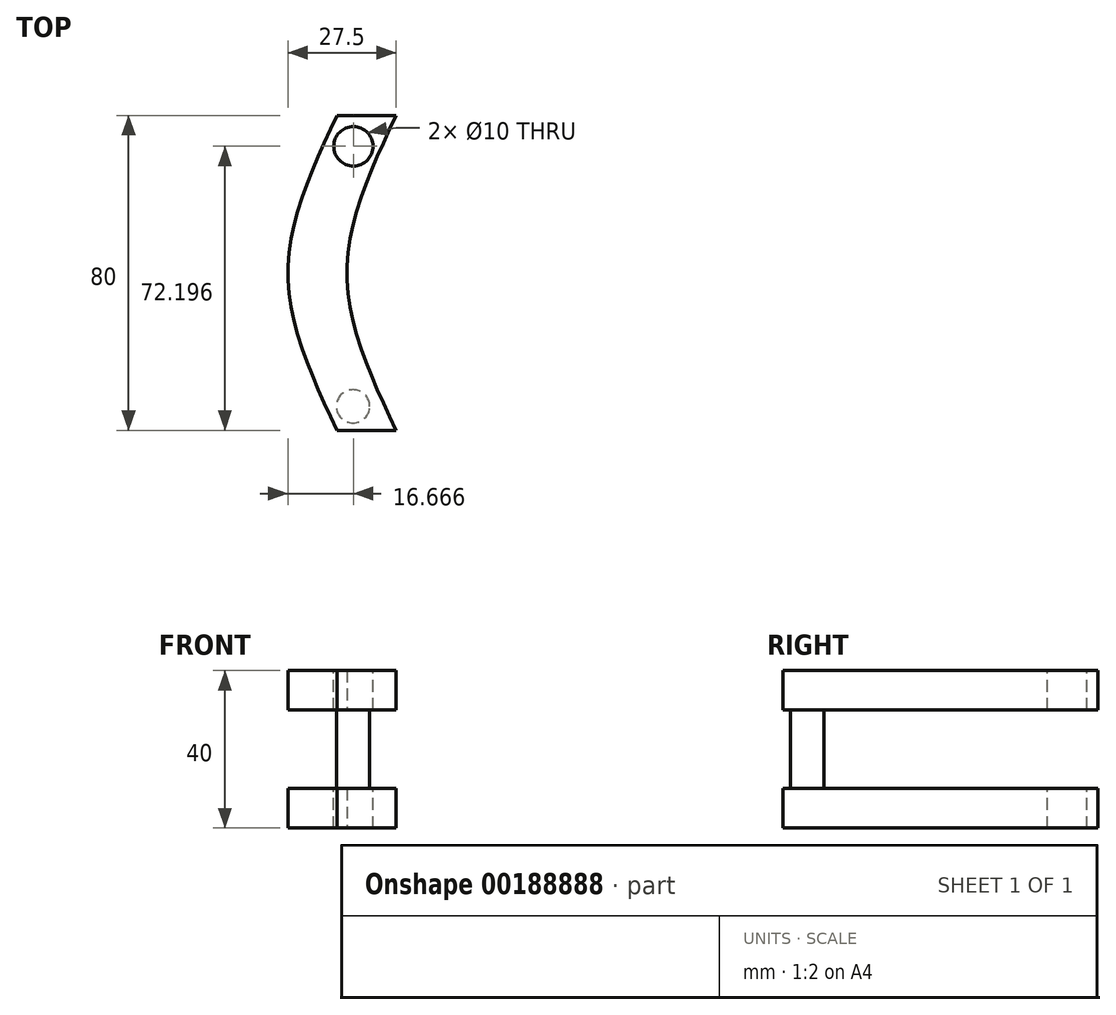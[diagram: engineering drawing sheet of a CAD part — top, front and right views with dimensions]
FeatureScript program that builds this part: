
annotation { "Feature Type Name" : "Feature", "Feature Type Description" : "" }
export const myFeature = defineFeature(function(context is Context, id is Id, definition is map)
    precondition{}
    {
        {
            var Q0;
            Q0=qCreatedBy(makeId("Front.planeOp"),FACE);
            var sketch = newSketch(context, id + "F0", { "sketchPlane" : qUnion([Q0])});
            skLineSegment(sketch, "E0.bottom", {"start": v(7.5, 10) * mm, "end": v(-7.5, 10) * mm});
            skLineSegment(sketch, "E0.top", {"start": v(7.5, 20) * mm, "end": v(-7.5, 20) * mm});
            skLineSegment(sketch, "E0.left", {"start": v(7.5, 10) * mm, "end": v(7.5, 20) * mm});
            skLineSegment(sketch, "E0.right", {"start": v(-7.5, 10) * mm, "end": v(-7.5, 20) * mm});
            skPoint(sketch, "E0.middle", {"position": v(0, 15) * mm});
            skLineSegment(sketch, "E1.bottom", {"start": v(7.5, -20) * mm, "end": v(-7.5, -20) * mm});
            skLineSegment(sketch, "E1.top", {"start": v(7.5, -10) * mm, "end": v(-7.5, -10) * mm});
            skLineSegment(sketch, "E1.left", {"start": v(7.5, -20) * mm, "end": v(7.5, -10) * mm});
            skLineSegment(sketch, "E1.right", {"start": v(-7.5, -20) * mm, "end": v(-7.5, -10) * mm});
            skPoint(sketch, "E1.middle", {"position": v(0, -15) * mm});
            skSolve(sketch);
        }
        {
            var Q0;
            Q0=qCreatedBy(makeId("Front.planeOp"),FACE);
            cPlane(context, id + "F1", {"entities" : qUnion([Q0]), "cplaneType" : CPlaneType.OFFSET, "offset" : 40 * mm, "width" : 150 * mm, "height" : 150 * mm});
        }
        {
            var Q0;
            Q0=qCreatedBy(id+"F1.planeOp",FACE);
            var sketch = newSketch(context, id + "F2", { "sketchPlane" : qUnion([Q0])});
            skLineSegment(sketch, "E2.bottom", {"start": v(-20, 10) * mm, "end": v(-5, 10) * mm});
            skLineSegment(sketch, "E2.top", {"start": v(-20, 20) * mm, "end": v(-5, 20) * mm});
            skLineSegment(sketch, "E2.left", {"start": v(-20, 10) * mm, "end": v(-20, 20) * mm});
            skLineSegment(sketch, "E2.right", {"start": v(-5, 10) * mm, "end": v(-5, 20) * mm});
            skPoint(sketch, "E2.middle", {"position": v(-12.5, 15) * mm});
            skLineSegment(sketch, "E3.bottom", {"start": v(-5, -20) * mm, "end": v(-20, -20) * mm});
            skLineSegment(sketch, "E3.top", {"start": v(-5, -10) * mm, "end": v(-20, -10) * mm});
            skLineSegment(sketch, "E3.left", {"start": v(-5, -20) * mm, "end": v(-5, -10) * mm});
            skLineSegment(sketch, "E3.right", {"start": v(-20, -20) * mm, "end": v(-20, -10) * mm});
            skPoint(sketch, "E3.middle", {"position": v(-12.5, -15) * mm});
            skSolve(sketch);
        }
        {
            var Q0;
            Q0=qCreatedBy(id+"F1.planeOp",FACE);
            cPlane(context, id + "F3", {"entities" : qUnion([Q0]), "cplaneType" : CPlaneType.OFFSET, "offset" : 40 * mm, "width" : 150 * mm, "height" : 150 * mm});
        }
        {
            var Q0;
            Q0=qCreatedBy(id+"F3.planeOp",FACE);
            var sketch = newSketch(context, id + "F4", { "sketchPlane" : qUnion([Q0])});
            skLineSegment(sketch, "E4.bottom", {"start": v(7.5, 10) * mm, "end": v(-7.5, 10) * mm});
            skLineSegment(sketch, "E4.top", {"start": v(7.5, 20) * mm, "end": v(-7.5, 20) * mm});
            skLineSegment(sketch, "E4.left", {"start": v(7.5, 10) * mm, "end": v(7.5, 20) * mm});
            skLineSegment(sketch, "E4.right", {"start": v(-7.5, 10) * mm, "end": v(-7.5, 20) * mm});
            skPoint(sketch, "E4.middle", {"position": v(0, 15) * mm});
            skLineSegment(sketch, "E5.bottom", {"start": v(7.5, -20) * mm, "end": v(-7.5, -20) * mm});
            skLineSegment(sketch, "E5.top", {"start": v(7.5, -10) * mm, "end": v(-7.5, -10) * mm});
            skLineSegment(sketch, "E5.left", {"start": v(7.5, -20) * mm, "end": v(7.5, -10) * mm});
            skLineSegment(sketch, "E5.right", {"start": v(-7.5, -20) * mm, "end": v(-7.5, -10) * mm});
            skPoint(sketch, "E5.middle", {"position": v(0, -15) * mm});
            skSolve(sketch);
        }
        {
            var Q0;
            Q0=makeQuery(id+"F4.imprint","IMPRINT",FACE,{"disambiguationData":[TD([[makeQuery(id+"F4.imprint","IMPRINT",EDGE,{"derivedFrom":sQuery(id+"F4.wireOp",EDGE,"E4.bottom")}),-1.0]])]});
            var Q1;
            Q1=makeQuery(id+"F2.imprint","IMPRINT",FACE,{"disambiguationData":[TD([[makeQuery(id+"F2.imprint","IMPRINT",EDGE,{"derivedFrom":sQuery(id+"F2.wireOp",EDGE,"E2.bottom")}),1.0]])]});
            var Q2;
            Q2=makeQuery(id+"F0.imprint","IMPRINT",FACE,{"disambiguationData":[TD([[makeQuery(id+"F0.imprint","IMPRINT",EDGE,{"derivedFrom":sQuery(id+"F0.wireOp",EDGE,"E0.bottom")}),-1.0]])]});
            loft(context, id + "F5", {"sheetProfilesArray" : [{ "sheetProfileEntities" : qUnion([Q0]) }, { "sheetProfileEntities" : qUnion([Q1]) }, { "sheetProfileEntities" : qUnion([Q2]) }]});
        }
        {
            var Q0;
            Q0=makeQuery(id+"F4.imprint","IMPRINT",FACE,{"disambiguationData":[TD([[makeQuery(id+"F4.imprint","IMPRINT",EDGE,{"derivedFrom":sQuery(id+"F4.wireOp",EDGE,"E5.bottom")}),-1.0]])]});
            var Q1;
            Q1=makeQuery(id+"F2.imprint","IMPRINT",FACE,{"disambiguationData":[TD([[makeQuery(id+"F2.imprint","IMPRINT",EDGE,{"derivedFrom":sQuery(id+"F2.wireOp",EDGE,"E3.bottom")}),-1.0]])]});
            var Q2;
            Q2=makeQuery(id+"F0.imprint","IMPRINT",FACE,{"disambiguationData":[TD([[makeQuery(id+"F0.imprint","IMPRINT",EDGE,{"derivedFrom":sQuery(id+"F0.wireOp",EDGE,"E1.bottom")}),-1.0]])]});
            loft(context, id + "F6", {"sheetProfilesArray" : [{ "sheetProfileEntities" : qUnion([Q0]) }, { "sheetProfileEntities" : qUnion([Q1]) }, { "sheetProfileEntities" : qUnion([Q2]) }]});
        }
        {
            var Q0;
            Q0=makeQuery(id+"F5.opLoft","SWEPT_FACE",FACE,{"disambiguationData":[OSD([sQuery(id+"F2.wireOp",EDGE,"E2.top"),sQuery(id+"F2.wireOp",EDGE,"E2.left"),sQuery(id+"F2.wireOp",EDGE,"E2.right"),sQuery(id+"F4.wireOp",EDGE,"E4.top"),sQuery(id+"F4.wireOp",EDGE,"E4.left"),sQuery(id+"F4.wireOp",EDGE,"E4.right")])]});
            var sketch = newSketch(context, id + "F7", { "sketchPlane" : qUnion([Q0])});
            skCircle(sketch, "E6", {"center": v(-3.43, -73.88) * mm, "radius": 4.22 * mm});
            skSolve(sketch);
        }
        {
            var Q0;
            Q0 = qSketchRegion(id + "F7", true);
            extrude(context, id + "F8", {"entities" : qUnion([Q0]), "operationType" : NewBodyOperationType.ADD, "oppositeDirection" : true, "depth" : 35 * mm});
        }
        {
            var Q0;
            Q0=makeQuery(id+"F5.opLoft","SWEPT_FACE",FACE,{"disambiguationData":[OSD([sQuery(id+"F2.wireOp",EDGE,"E2.top"),sQuery(id+"F2.wireOp",EDGE,"E2.left"),sQuery(id+"F2.wireOp",EDGE,"E2.right"),sQuery(id+"F4.wireOp",EDGE,"E4.top"),sQuery(id+"F4.wireOp",EDGE,"E4.left"),sQuery(id+"F4.wireOp",EDGE,"E4.right")])]});
            var sketch = newSketch(context, id + "F9", { "sketchPlane" : qUnion([Q0])});
            skCircle(sketch, "E7", {"center": v(-3.33, -7.8) * mm, "radius": 5 * mm});
            skSolve(sketch);
        }
        {
            var Q0;
            Q0 = qSketchRegion(id + "F9", true);
            extrude(context, id + "F10", {"entities" : qUnion([Q0]), "operationType" : NewBodyOperationType.REMOVE, "oppositeDirection" : true, "depth" : 50 * mm});
        }
    });
